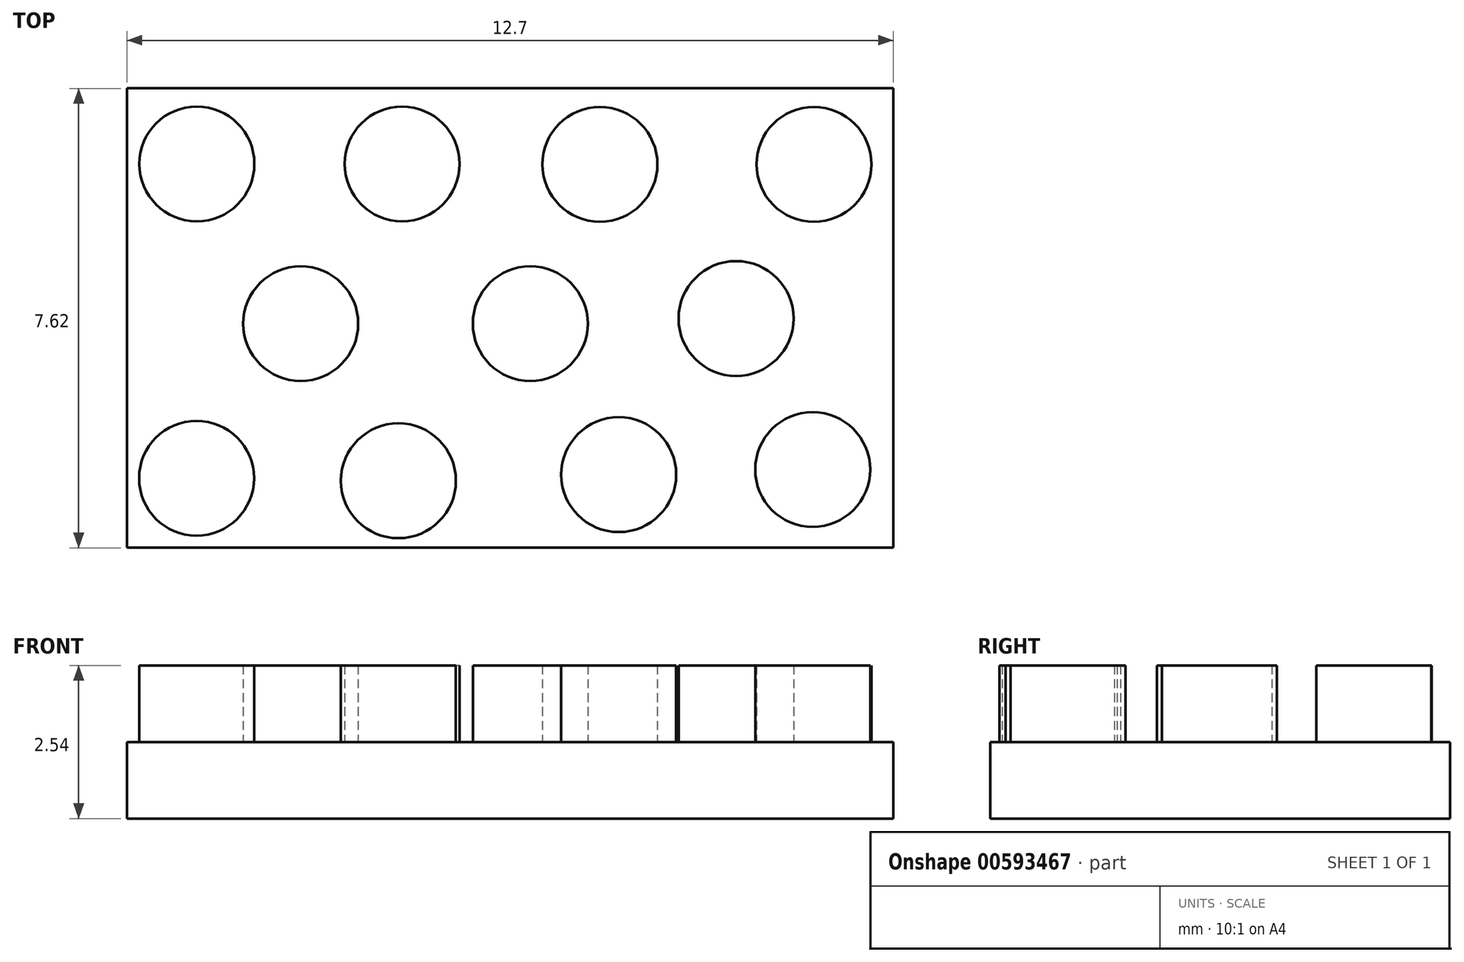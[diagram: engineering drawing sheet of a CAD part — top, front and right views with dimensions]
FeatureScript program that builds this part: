
annotation { "Feature Type Name" : "Feature", "Feature Type Description" : "" }
export const myFeature = defineFeature(function(context is Context, id is Id, definition is map)
    precondition{}
    {
        {
            var Q0;
            Q0=qCreatedBy(makeId("Top.planeOp"),FACE);
            var sketch = newSketch(context, id + "F0", { "sketchPlane" : qUnion([Q0])});
            skLineSegment(sketch, "E0.bottom", {"start": v(-40.33, -18.26) * mm, "end": v(-27.63, -18.26) * mm});
            skLineSegment(sketch, "E0.top", {"start": v(-40.33, -10.64) * mm, "end": v(-27.63, -10.64) * mm});
            skLineSegment(sketch, "E0.left", {"start": v(-40.33, -18.26) * mm, "end": v(-40.33, -10.64) * mm});
            skLineSegment(sketch, "E0.right", {"start": v(-27.63, -18.26) * mm, "end": v(-27.63, -10.64) * mm});
            skSolve(sketch);
        }
        {
            var Q0;
            Q0=makeQuery(id+"F0.imprint","IMPRINT",FACE,{"disambiguationData":[TD([[makeQuery(id+"F0.imprint","IMPRINT",EDGE,{"derivedFrom":sQuery(id+"F0.wireOp",EDGE,"E0.bottom")}),1.0]])]});
            extrude(context, id + "F1", {"entities" : qUnion([Q0]), "depth" : 1.27 * mm, "offsetDistance" : 25.4 * mm});
        }
        {
            var Q0;
            Q0=makeQuery(id+"F1.opExtrude","CAP_FACE",FACE,{"disambiguationData":[OSD([sQuery(id+"F0.wireOp",EDGE,"E0.bottom"),sQuery(id+"F0.wireOp",EDGE,"E0.top"),sQuery(id+"F0.wireOp",EDGE,"E0.left"),sQuery(id+"F0.wireOp",EDGE,"E0.right")])],"isStart":false});
            var sketch = newSketch(context, id + "F2", { "sketchPlane" : qUnion([Q0])});
            skCircle(sketch, "E1", {"center": v(-39.17, -11.9) * mm, "radius": 0.95 * mm});
            skCircle(sketch, "E2", {"center": v(-35.77, -11.9) * mm, "radius": 0.95 * mm});
            skCircle(sketch, "E3", {"center": v(-39.18, -17.1) * mm, "radius": 0.95 * mm});
            skCircle(sketch, "E4", {"center": v(-32.18, -17.05) * mm, "radius": 0.95 * mm});
            skCircle(sketch, "E5", {"center": v(-35.83, -17.15) * mm, "radius": 0.95 * mm});
            skCircle(sketch, "E6", {"center": v(-32.5, -11.9) * mm, "radius": 0.95 * mm});
            skCircle(sketch, "E7", {"center": v(-28.95, -11.9) * mm, "radius": 0.95 * mm});
            skCircle(sketch, "E8", {"center": v(-28.97, -16.96) * mm, "radius": 0.95 * mm});
            skCircle(sketch, "E9", {"center": v(-30.24, -14.46) * mm, "radius": 0.95 * mm});
            skCircle(sketch, "E10", {"center": v(-37.45, -14.54) * mm, "radius": 0.95 * mm});
            skCircle(sketch, "E11", {"center": v(-33.65, -14.54) * mm, "radius": 0.95 * mm});
            skSolve(sketch);
        }
        {
            var Q0;
            Q0 = qSketchRegion(id + "F2", true);
            extrude(context, id + "F3", {"entities" : qUnion([Q0]), "operationType" : NewBodyOperationType.ADD, "depth" : 1.27 * mm, "offsetDistance" : 25.4 * mm});
        }
    });
